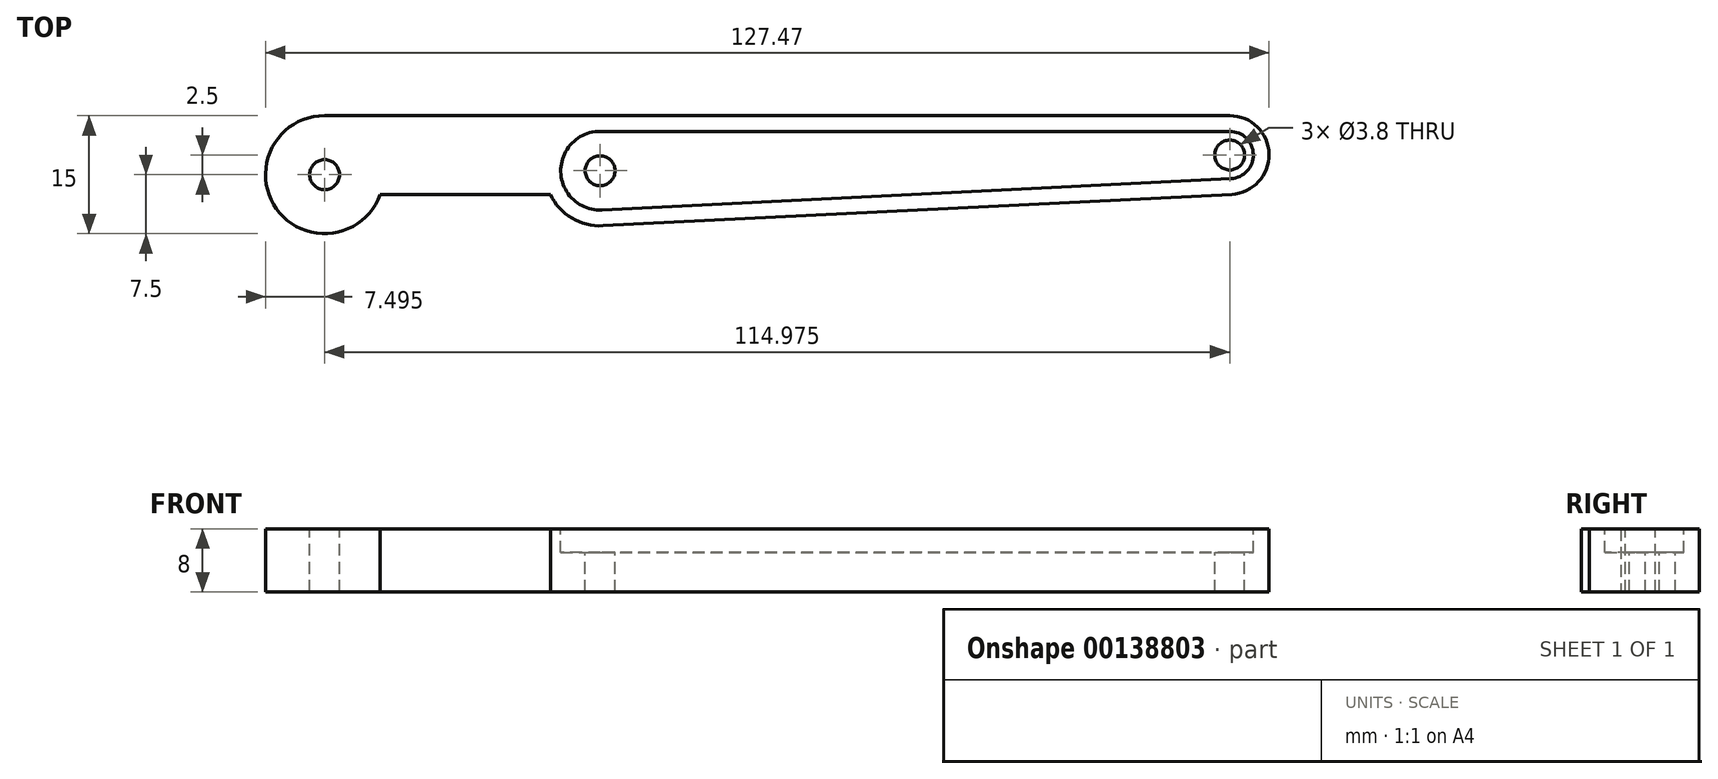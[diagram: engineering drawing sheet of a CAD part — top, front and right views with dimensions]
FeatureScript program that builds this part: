
annotation { "Feature Type Name" : "Feature", "Feature Type Description" : "" }
export const myFeature = defineFeature(function(context is Context, id is Id, definition is map)
    precondition{}
    {
        {
            var Q0;
            Q0=qCreatedBy(makeId("Top.planeOp"),FACE);
            var sketch = newSketch(context, id + "F0", { "sketchPlane" : qUnion([Q0])});
            skCircle(sketch, "E0", {"center": v(0, 0) * mm, "radius": 5 * mm});
            skCircle(sketch, "E1", {"center": v(-2, 79.97) * mm, "radius": 7 * mm});
            skLineSegment(sketch, "E2", {"start": v(-2, 79.97) * mm, "end": v(0, 0) * mm});
            skLineSegment(sketch, "E3", {"start": v(5, 79.97) * mm, "end": v(5, 0) * mm});
            skLineSegment(sketch, "E4", {"start": v(-9, 79.63) * mm, "end": v(-5, -0.25) * mm});
            skLineSegment(sketch, "E5.bottom", {"start": v(5, 79.97) * mm, "end": v(-5, 79.97) * mm});
            skLineSegment(sketch, "E5.top", {"start": v(5, 114.97) * mm, "end": v(-5, 114.97) * mm});
            skLineSegment(sketch, "E5.left", {"start": v(5, 79.97) * mm, "end": v(5, 114.97) * mm});
            skLineSegment(sketch, "E5.right", {"start": v(-5, 79.97) * mm, "end": v(-5, 114.97) * mm});
            skCircle(sketch, "E6", {"center": v(-2.5, 114.97) * mm, "radius": 7.5 * mm});
            skSolve(sketch);
        }
        {
            var Q0;
            Q0=qSketchRegion(id+"F0",true);
            extrude(context, id + "F1", {"entities" : qUnion([Q0]), "depth" : 8 * mm});
        }
        {
            var Q0;
            Q0=makeQuery(id+"F1.opExtrude","CAP_FACE",FACE,{"disambiguationData":[OSD([sQuery(id+"F0.wireOp",EDGE,"E0"),sQuery(id+"F0.wireOp",EDGE,"E1"),sQuery(id+"F0.wireOp",EDGE,"E3"),sQuery(id+"F0.wireOp",EDGE,"E4"),sQuery(id+"F0.wireOp",EDGE,"E5.left"),sQuery(id+"F0.wireOp",EDGE,"E5.right"),sQuery(id+"F0.wireOp",EDGE,"E6")])],"isStart":false});
            var sketch = newSketch(context, id + "F2", { "sketchPlane" : qUnion([Q0])});
            skCircle(sketch, "E7", {"center": v(0, 0) * mm, "radius": 1.9 * mm});
            skCircle(sketch, "E8", {"center": v(-2, 79.97) * mm, "radius": 1.9 * mm});
            skCircle(sketch, "E9", {"center": v(-2.5, 114.97) * mm, "radius": 1.9 * mm});
            skSolve(sketch);
        }
        {
            var Q0;
            Q0=makeQuery(id+"F2.imprint","IMPRINT",FACE,{"disambiguationData":[TD([[makeQuery(id+"F2.imprint","IMPRINT",EDGE,{"derivedFrom":sQuery(id+"F2.wireOp",EDGE,"E8")}),1.0]])]});
            var Q1;
            Q1=makeQuery(id+"F2.imprint","IMPRINT",FACE,{"disambiguationData":[TD([[makeQuery(id+"F2.imprint","IMPRINT",EDGE,{"derivedFrom":sQuery(id+"F2.wireOp",EDGE,"E9")}),1.0]])]});
            var Q2;
            Q2=makeQuery(id+"F2.imprint","IMPRINT",FACE,{"disambiguationData":[TD([[makeQuery(id+"F2.imprint","IMPRINT",EDGE,{"derivedFrom":sQuery(id+"F2.wireOp",EDGE,"E7")}),1.0]])]});
            extrude(context, id + "F3", {"entities" : qUnion([Q0, Q1, Q2]), "operationType" : NewBodyOperationType.REMOVE, "endBound" : BoundingType.THROUGH_ALL, "oppositeDirection" : true, "depth" : 25 * mm});
        }
        {
            var Q0;
            Q0=makeQuery(id+"F1.opExtrude","CAP_FACE",FACE,{"disambiguationData":[OSD([sQuery(id+"F0.wireOp",EDGE,"E0"),sQuery(id+"F0.wireOp",EDGE,"E1"),sQuery(id+"F0.wireOp",EDGE,"E3"),sQuery(id+"F0.wireOp",EDGE,"E4"),sQuery(id+"F0.wireOp",EDGE,"E5.left"),sQuery(id+"F0.wireOp",EDGE,"E5.right"),sQuery(id+"F0.wireOp",EDGE,"E6")])],"isStart":false});
            var sketch = newSketch(context, id + "F4", { "sketchPlane" : qUnion([Q0])});
            skLineSegment(sketch, "E10.0", {"start": v(3, 0) * mm, "end": v(3, 79.97) * mm});
            skArc(sketch, "E10.1", {"start": v(-3, -0.15) * mm, "mid": v(0.08, -3) * mm, "end": v(3, 0) * mm});
            skLineSegment(sketch, "E10.2", {"start": v(-7, 79.73) * mm, "end": v(-3, -0.15) * mm});
            skArc(sketch, "E10.3", {"start": v(-4.14, 84.5) * mm, "mid": v(-6.3, 82.54) * mm, "end": v(-7, 79.73) * mm});
            skArc(sketch, "E11", {"start": v(3, 79.97) * mm, "mid": v(-2.13, 84.97) * mm, "end": v(-7, 79.73) * mm});
            skSolve(sketch);
        }
        {
            var Q0;
            Q0=qSketchRegion(id+"F4",true);
            extrude(context, id + "F5", {"entities" : qUnion([Q0]), "operationType" : NewBodyOperationType.REMOVE, "oppositeDirection" : true, "depth" : 3 * mm});
        }
        {
            var Q0;
            Q0=makeQuery(id+"F1.opExtrude","SWEPT_BODY",BODY,{"disambiguationData":[OSD([sQuery(id+"F0.wireOp",EDGE,"E0"),sQuery(id+"F0.wireOp",EDGE,"E1"),sQuery(id+"F0.wireOp",EDGE,"E3"),sQuery(id+"F0.wireOp",EDGE,"E4"),sQuery(id+"F0.wireOp",EDGE,"E5.left"),sQuery(id+"F0.wireOp",EDGE,"E5.right"),sQuery(id+"F0.wireOp",EDGE,"E6")])]});
            var Q1;
            Q1=makeQuery(id+"F5.boolean.opBoolean","INTERSECT",EDGE,{"derivedFrom":[makeQuery(id+"F3.boolean.opBoolean","COPY",FACE,{"derivedFrom":makeQuery(id+"F3.opExtrude","SWEPT_FACE",FACE,{"disambiguationData":[OSD([sQuery(id+"F2.wireOp",EDGE,"E7")])]})}),makeQuery(id+"F5.opExtrude","CAP_FACE",FACE,{"disambiguationData":[OSD([sQuery(id+"F4.wireOp",EDGE,"E10.0"),sQuery(id+"F4.wireOp",EDGE,"E10.1"),sQuery(id+"F4.wireOp",EDGE,"E10.2"),sQuery(id+"F4.wireOp",EDGE,"E11")])],"isStart":false})]});
            transform(context, id + "F6", {"entities" : qUnion([Q0]), "transformType" : TransformType.ROTATION, "transformAxis" : qUnion([Q1]), "angle" : 90 * degree, "makeCopy" : false});
        }
    });
